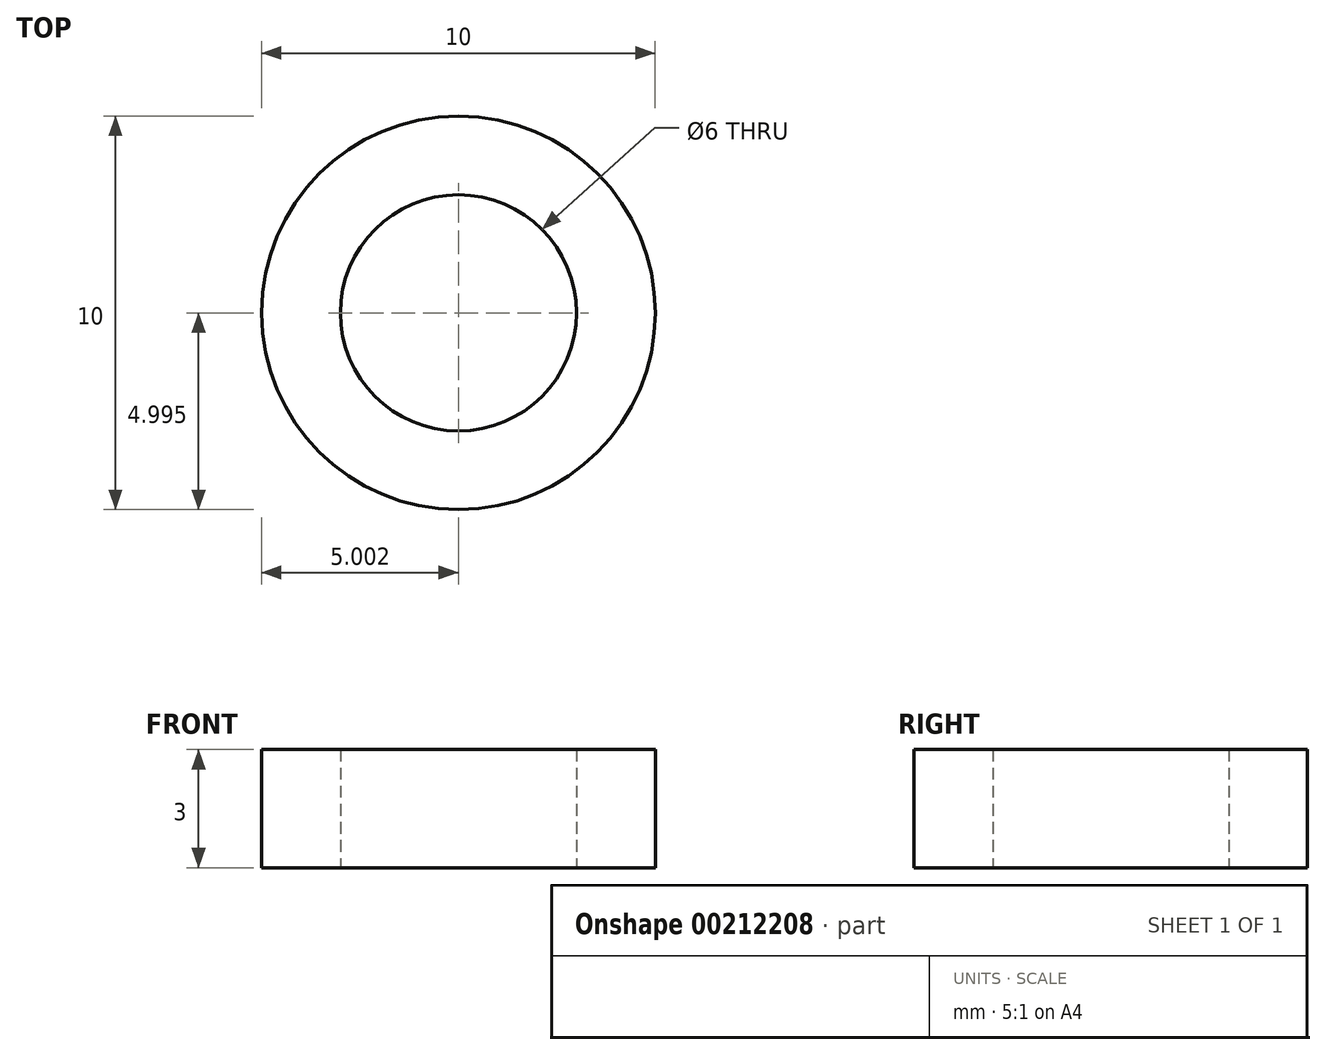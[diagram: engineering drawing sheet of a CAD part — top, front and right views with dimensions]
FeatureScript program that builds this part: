
annotation { "Feature Type Name" : "Feature", "Feature Type Description" : "" }
export const myFeature = defineFeature(function(context is Context, id is Id, definition is map)
    precondition{}
    {
        {
            var Q0;
            Q0=qCreatedBy(makeId("Top.planeOp"),FACE);
            var sketch = newSketch(context, id + "F0", { "sketchPlane" : qUnion([Q0])});
            skCircle(sketch, "E0", {"center": v(-35.96, 37.54) * mm, "radius": 5 * mm});
            skCircle(sketch, "E1", {"center": v(-35.96, 37.54) * mm, "radius": 3 * mm});
            skSolve(sketch);
        }
        {
            var Q0;
            Q0 = qSketchRegion(id + "F0", true);
            extrude(context, id + "F1", {"entities" : qUnion([Q0]), "depth" : 3 * mm});
        }
    });
